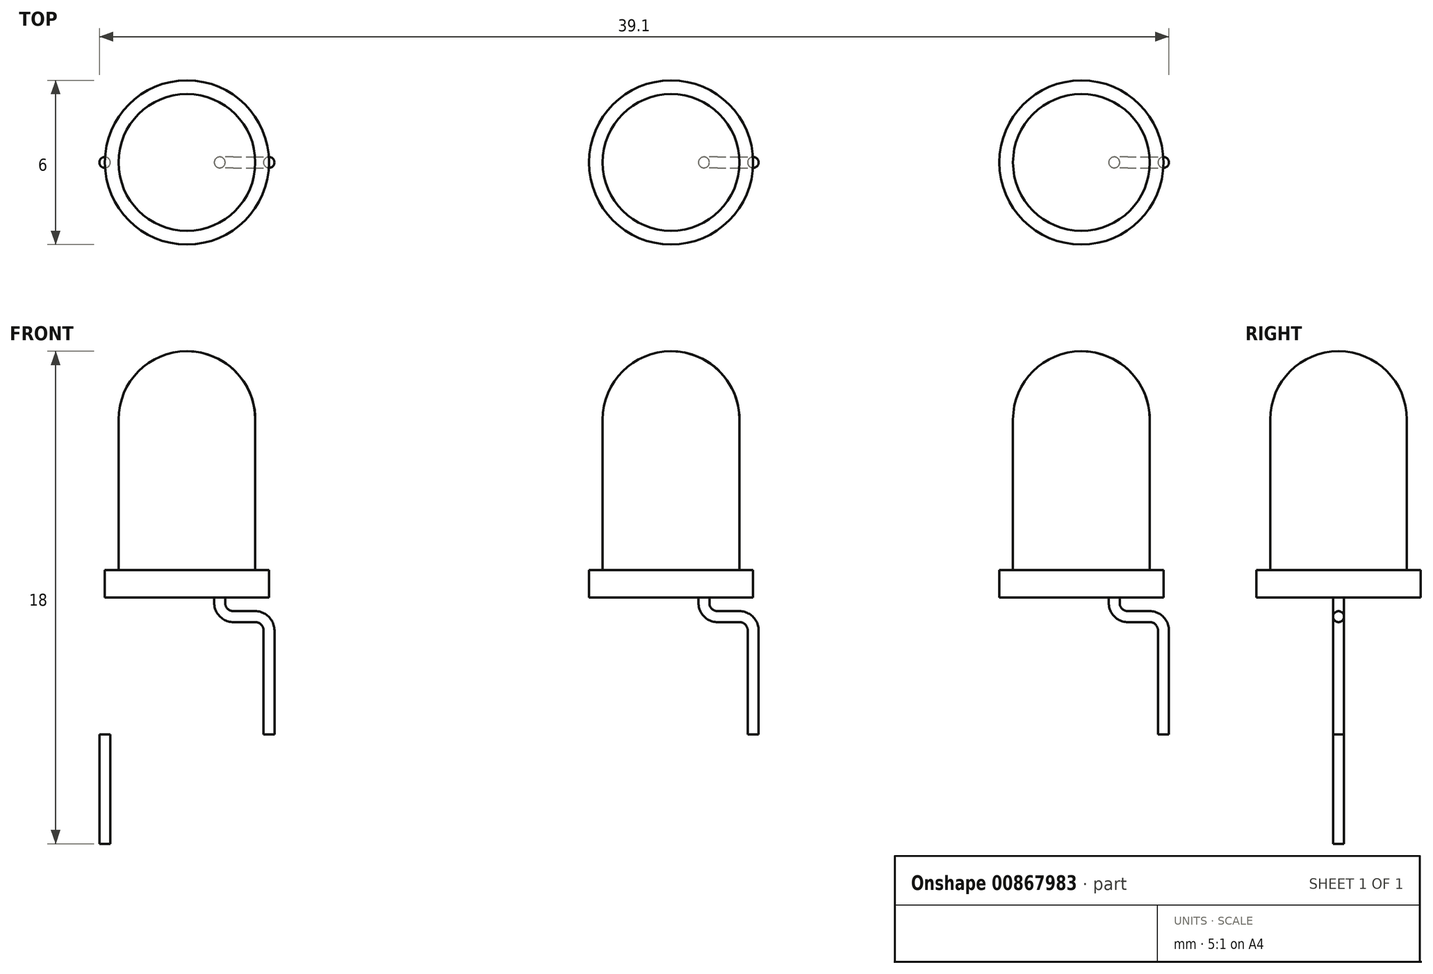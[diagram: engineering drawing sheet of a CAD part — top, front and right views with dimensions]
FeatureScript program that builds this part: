
annotation { "Feature Type Name" : "Feature", "Feature Type Description" : "" }
export const myFeature = defineFeature(function(context is Context, id is Id, definition is map)
    precondition{}
    {
        {
            var Q0;
            Q0=qCreatedBy(makeId("Front.planeOp"),FACE);
            var sketch = newSketch(context, id + "F0", { "sketchPlane" : qUnion([Q0])});
            skCircle(sketch, "E0", {"center": v(0, 6.5) * mm, "radius": 2.5 * mm});
            skLineSegment(sketch, "E1", {"start": v(2.5, 6.5) * mm, "end": v(2.5, 1) * mm});
            skLineSegment(sketch, "E2", {"start": v(2.5, 1) * mm, "end": v(3, 1) * mm});
            skLineSegment(sketch, "E3", {"start": v(3, 1) * mm, "end": v(3, 0) * mm});
            skLineSegment(sketch, "E4", {"start": v(3, 0) * mm, "end": v(0, 0) * mm});
            skLineSegment(sketch, "E5", {"start": v(0, 6.5) * mm, "end": v(0, 0) * mm});
            skLineSegment(sketch, "E6", {"start": v(0, 6.5) * mm, "end": v(0, 9) * mm});
            skSolve(sketch);
        }
        {
            var Q0;
            {var subQ0=sQuery(id+"F0.wireOp",EDGE,"E1");Q0=makeQuery(id+"F0.imprint","IMPRINT",FACE,{"disambiguationData":[TD([[makeQuery(id+"F0.imprint","IMPRINT",EDGE,{"derivedFrom":subQ0}),-1.0]])]});}
            var Q1;
            {var subQ2=sQuery(id+"F0.wireOp",EDGE,"E6");Q1=makeQuery(id+"F0.imprint","IMPRINT",FACE,{"disambiguationData":[TD([[makeQuery(id+"F0.imprint","IMPRINT",EDGE,{"derivedFrom":subQ2}),-1.0]])]});}
            var Q2;
            Q2=sQuery(id+"F0.wireOp",EDGE,"E5");
            revolve(context, id + "F1", {"surfaceOperationType" : NewSurfaceOperationType.NEW, "entities" : qUnion([Q0, Q1]), "axis" : qUnion([Q2]), "revolveType" : RevolveType.FULL});
        }
        {
            var Q0;
            Q0=qCreatedBy(makeId("Front.planeOp"),FACE);
            var sketch = newSketch(context, id + "F2", { "sketchPlane" : qUnion([Q0])});
            skLineSegment(sketch, "E7", {"start": v(1.2, 0) * mm, "end": v(1.2, -0.2) * mm});
            skLineSegment(sketch, "E8", {"start": v(-1.2, 0) * mm, "end": v(-1.2, -0.2) * mm});
            skLineSegment(sketch, "E9", {"start": v(1.7, -0.7) * mm, "end": v(2.5, -0.7) * mm});
            skLineSegment(sketch, "E10", {"start": v(-1.7, -0.7) * mm, "end": v(-2.5, -0.7) * mm});
            skLineSegment(sketch, "E11", {"start": v(-3, -1.2) * mm, "end": v(-3, -5) * mm});
            skLineSegment(sketch, "E12", {"start": v(3, -1.2) * mm, "end": v(3, -5) * mm});
            skArc(sketch, "E13", {"start": v(-2.5, -0.7) * mm, "mid": v(-2.85, -0.85) * mm, "end": v(-3, -1.2) * mm});
            skArc(sketch, "E14", {"start": v(-1.7, -0.7) * mm, "mid": v(-1.35, -0.55) * mm, "end": v(-1.2, -0.2) * mm});
            skArc(sketch, "E15", {"start": v(1.2, -0.2) * mm, "mid": v(1.35, -0.55) * mm, "end": v(1.7, -0.7) * mm});
            skArc(sketch, "E16", {"start": v(3, -1.2) * mm, "mid": v(2.85, -0.85) * mm, "end": v(2.5, -0.7) * mm});
            skLineSegment(sketch, "E17", {"start": v(-1.2, 0) * mm, "end": v(1.2, 0) * mm, "construction": true});
            skLineSegment(sketch, "E18", {"start": v(0, 0) * mm, "end": v(0, -5) * mm, "construction": true});
            skLineSegment(sketch, "E19", {"start": v(0, -5) * mm, "end": v(3, -5) * mm, "construction": true});
            skLineSegment(sketch, "E20", {"start": v(0, -5) * mm, "end": v(-3, -5) * mm, "construction": true});
            skSolve(sketch);
        }
        {
            var Q0;
            Q0=qCreatedBy(makeId("Top.planeOp"),FACE);
            var sketch = newSketch(context, id + "F3", { "sketchPlane" : qUnion([Q0])});
            skCircle(sketch, "E21", {"center": v(1.2, 0) * mm, "radius": 0.2 * mm});
            skSolve(sketch);
        }
        {
            var Q0;
            Q0 = qSketchRegion(id + "F3", true);
            var Q1;
            Q1=sQuery(id+"F2.wireOp",EDGE,"E7");
            var Q2;
            Q2=sQuery(id+"F2.wireOp",EDGE,"E15");
            var Q3;
            Q3=sQuery(id+"F2.wireOp",EDGE,"E9");
            var Q4;
            Q4=sQuery(id+"F2.wireOp",EDGE,"E16");
            var Q5;
            Q5=sQuery(id+"F2.wireOp",EDGE,"E12");
            sweep(context, id + "F4", {"operationType" : NewBodyOperationType.ADD, "profiles" : qUnion([Q0]), "path" : qUnion([Q1, Q2, Q3, Q4, Q5])});
        }
        {
            var Q0;
            Q0=makeQuery(id+"F4.opSweep","CAP_FACE",FACE,{"disambiguationData":[OSD([sQuery(id+"F2.wireOp",VERTEX,"E12.end"),sQuery(id+"F3.wireOp",EDGE,"E21")])],"isStart":false});
            var sketch = newSketch(context, id + "F5", { "sketchPlane" : qUnion([Q0])});
            skCircle(sketch, "E22", {"center": v(-3, 0) * mm, "radius": 0.2 * mm});
            skSolve(sketch);
        }
        {
            var Q0;
            Q0 = qSketchRegion(id + "F5", true);
            extrude(context, id + "F6", {"entities" : qUnion([Q0]), "operationType" : NewBodyOperationType.ADD, "depth" : 4 * mm, "offsetDistance" : 25 * mm});
        }
        {
            var Q0;
            Q0=makeQuery(id+"F1.opRevolve","SWEPT_BODY",BODY,{"disambiguationData":[OSD([sQuery(id+"F0.wireOp",EDGE,"E0"),sQuery(id+"F0.wireOp",EDGE,"E1"),sQuery(id+"F0.wireOp",EDGE,"E2"),sQuery(id+"F0.wireOp",EDGE,"E3"),sQuery(id+"F0.wireOp",EDGE,"E4"),sQuery(id+"F0.wireOp",EDGE,"E5"),sQuery(id+"F0.wireOp",EDGE,"E6")])]});
            transform(context, id + "F7", {"entities" : qUnion([Q0]), "transformType" : TransformType.TRANSLATION_3D, "dx" : 17.7 * mm, "dy" : 0 * mm, "dz" : 0 * mm, "makeCopy" : true});
        }
        {
            var Q0;
            Q0=makeQuery(id+"F1.opRevolve","SWEPT_BODY",BODY,{"disambiguationData":[OSD([sQuery(id+"F0.wireOp",EDGE,"E0"),sQuery(id+"F0.wireOp",EDGE,"E1"),sQuery(id+"F0.wireOp",EDGE,"E2"),sQuery(id+"F0.wireOp",EDGE,"E3"),sQuery(id+"F0.wireOp",EDGE,"E4"),sQuery(id+"F0.wireOp",EDGE,"E5"),sQuery(id+"F0.wireOp",EDGE,"E6")])]});
            transform(context, id + "F8", {"entities" : qUnion([Q0]), "transformType" : TransformType.TRANSLATION_3D, "dx" : 32.7 * mm, "dy" : 0 * mm, "dz" : 0 * mm, "makeCopy" : true});
        }
    });
